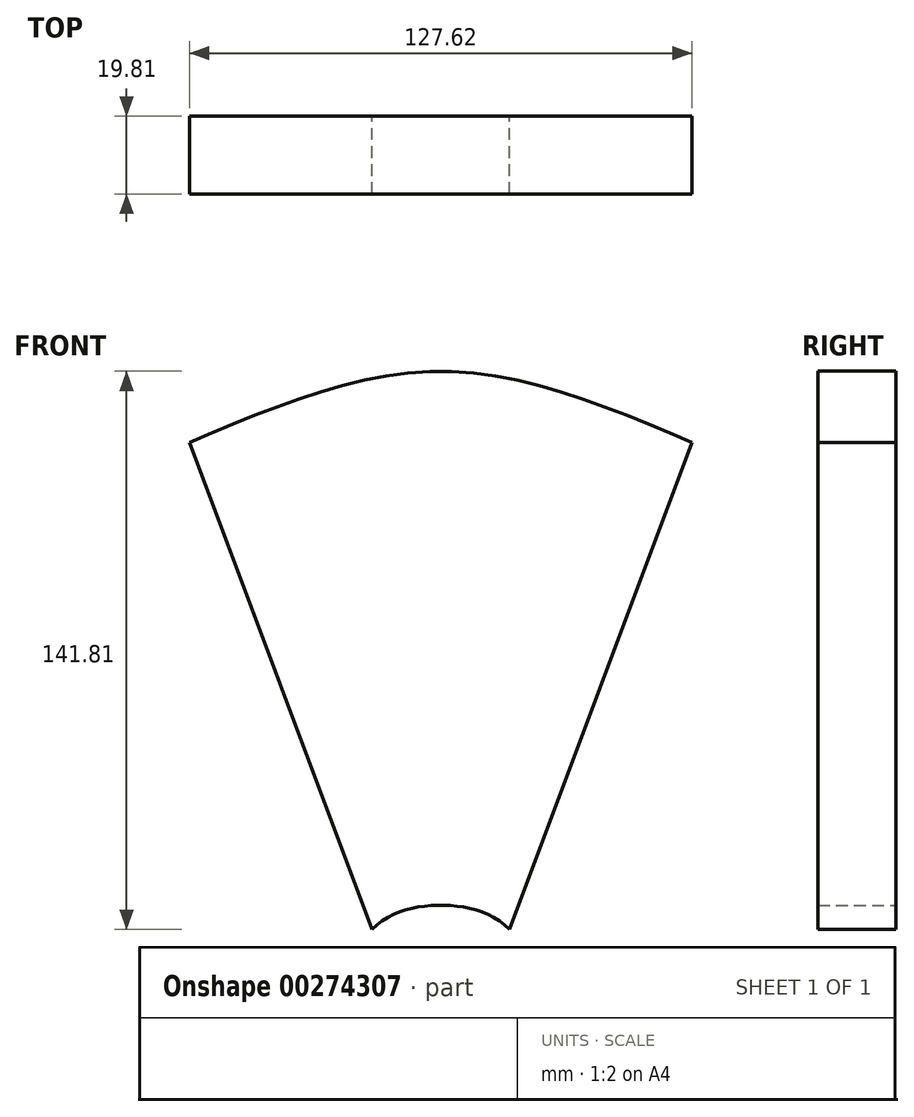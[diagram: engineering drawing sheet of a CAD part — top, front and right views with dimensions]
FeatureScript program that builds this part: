
annotation { "Feature Type Name" : "Feature", "Feature Type Description" : "" }
export const myFeature = defineFeature(function(context is Context, id is Id, definition is map)
    precondition{}
    {
        {
            var Q0;
            Q0=qCreatedBy(makeId("Front.planeOp"),FACE);
            var sketch = newSketch(context, id + "F0", { "sketchPlane" : qUnion([Q0])});
            skLineSegment(sketch, "E0", {"start": v(-63.8, 17.02) * mm, "end": v(-17.5, -106.67) * mm});
            skLineSegment(sketch, "E1.MirrorCS", {"start": v(63.8, 17.02) * mm, "end": v(17.5, -106.67) * mm});
            skFitSpline(sketch, "E2", {"points": [v(-17.5, -106.67) * mm, v(0, -100.56) * mm, v(17.5, -106.67) * mm], "startDerivative": vector(28.83, 28.62) * mm, "endDerivative": vector(28.83, -28.62) * mm});
            skFitSpline(sketch, "E3", {"points": [v(-63.8, 17.02) * mm, v(0, 35.14) * mm, v(63.8, 17.02) * mm], "startDerivative": vector(127.62, 54.34) * mm, "endDerivative": vector(127.62, -54.34) * mm});
            skSolve(sketch);
        }
        {
            var Q0;
            Q0=makeQuery(id+"F0.imprint","IMPRINT",FACE,{"disambiguationData":[TD([[makeQuery(id+"F0.imprint","IMPRINT",EDGE,{"derivedFrom":sQuery(id+"F0.wireOp",EDGE,"E0")}),1.0]])]});
            extrude(context, id + "F1", {"entities" : qUnion([Q0]), "depth" : 19.8 * mm});
        }
        {
            var Q0;
            Q0=makeQuery(id+"F1.opExtrude","CAP_FACE",FACE,{"disambiguationData":[OSD([sQuery(id+"F0.wireOp",EDGE,"E0"),sQuery(id+"F0.wireOp",EDGE,"E1.MirrorCS"),sQuery(id+"F0.wireOp",EDGE,"E2"),sQuery(id+"F0.wireOp",EDGE,"E3")])],"isStart":false});
            var sketch = newSketch(context, id + "F2", { "sketchPlane" : qUnion([Q0])});
            skLineSegment(sketch, "E4", {"start": v(-40.66, -44.82) * mm, "end": v(-45.1, -32.93) * mm});
            skLineSegment(sketch, "E5", {"start": v(-40.66, -44.82) * mm, "end": v(-35.9, -57.52) * mm});
            skLineSegment(sketch, "E6.MirrorCS", {"start": v(40.66, -44.82) * mm, "end": v(35.9, -57.52) * mm});
            skLineSegment(sketch, "E7.MirrorCS", {"start": v(40.66, -44.82) * mm, "end": v(45.1, -32.93) * mm});
            skFitSpline(sketch, "E8", {"points": [v(-45.1, -32.93) * mm, v(0, -22.36) * mm, v(45.1, -32.93) * mm], "startDerivative": vector(90.22, 30.01) * mm, "endDerivative": vector(90.22, -30.01) * mm});
            skFitSpline(sketch, "E9", {"points": [v(-35.9, -57.52) * mm, v(0, -47.76) * mm, v(35.9, -57.52) * mm], "startDerivative": vector(71.8, 29.3) * mm, "endDerivative": vector(71.8, -29.3) * mm});
            skLineSegment(sketch, "E10", {"start": v(0, -22.36) * mm, "end": v(0, -47.76) * mm});
            skPoint(sketch, "E11", {"position": v(0, -35.06) * mm});
            skSolve(sketch);
        }
    });
